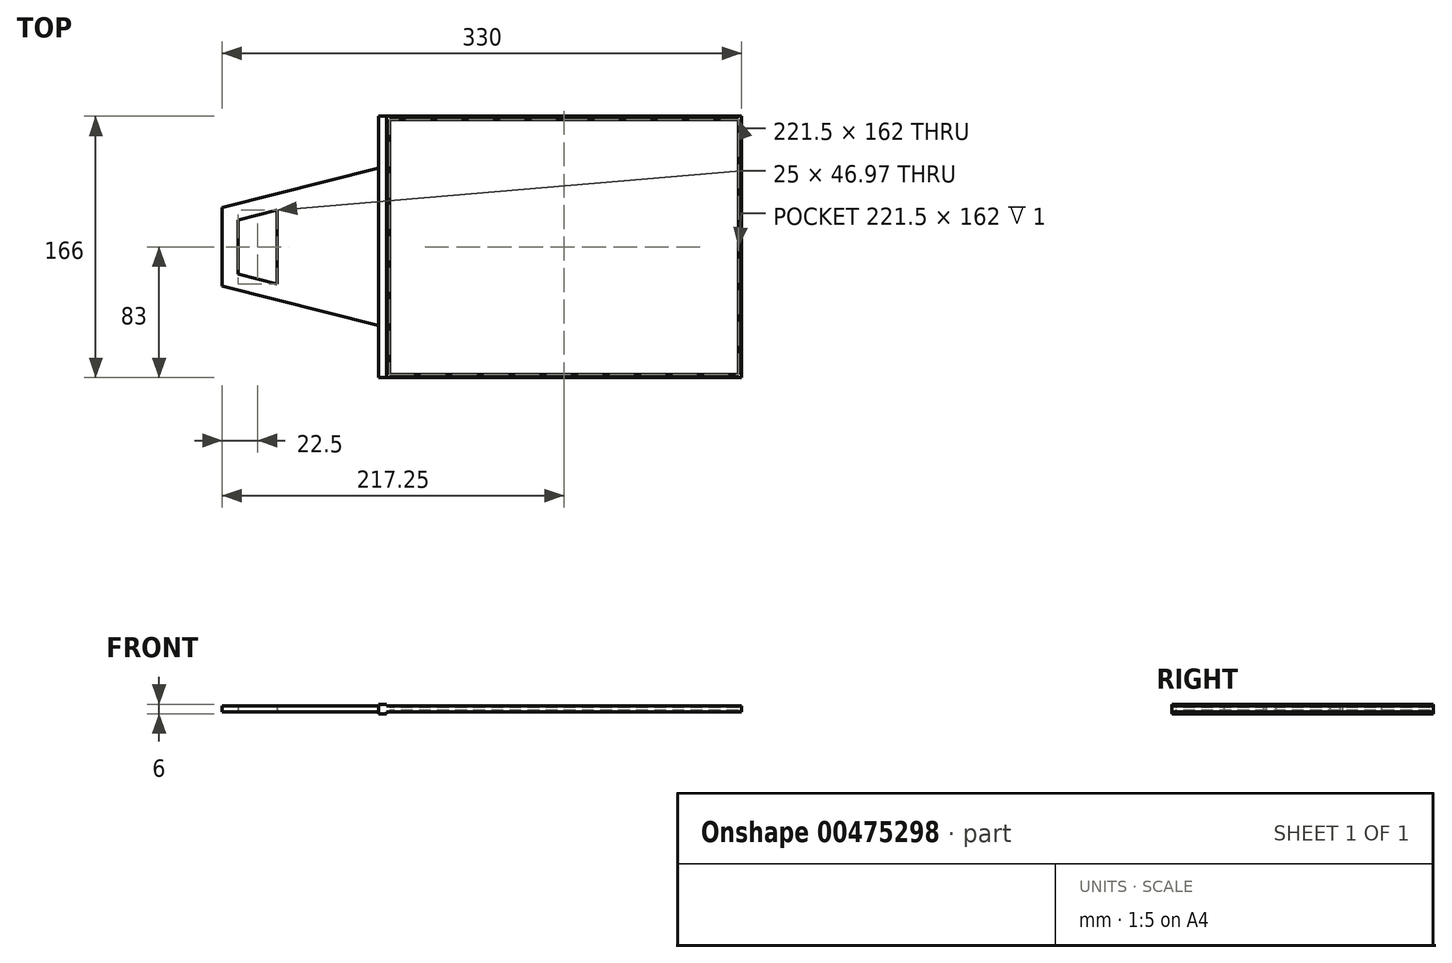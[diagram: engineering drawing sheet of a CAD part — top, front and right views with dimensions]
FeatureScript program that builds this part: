
annotation { "Feature Type Name" : "Feature", "Feature Type Description" : "" }
export const myFeature = defineFeature(function(context is Context, id is Id, definition is map)
    precondition{}
    {
        {
            var Q0;
            Q0=qCreatedBy(makeId("Top.planeOp"),FACE);
            var sketch = newSketch(context, id + "F0", { "sketchPlane" : qUnion([Q0])});
            skLineSegment(sketch, "E0.bottom", {"start": v(112.75, 83) * mm, "end": v(-112.75, 83) * mm});
            skLineSegment(sketch, "E0.top", {"start": v(112.75, -83) * mm, "end": v(-112.75, -83) * mm});
            skLineSegment(sketch, "E0.left", {"start": v(112.75, 83) * mm, "end": v(112.75, -83) * mm});
            skLineSegment(sketch, "E0.right", {"start": v(-112.75, 83) * mm, "end": v(-112.75, -83) * mm});
            skPoint(sketch, "E0.middle", {"position": v(0, 0) * mm});
            skLineSegment(sketch, "E1.bottom", {"start": v(110.75, 81) * mm, "end": v(-110.75, 81) * mm});
            skLineSegment(sketch, "E1.top", {"start": v(110.75, -81) * mm, "end": v(-110.75, -81) * mm});
            skLineSegment(sketch, "E1.left", {"start": v(110.75, 81) * mm, "end": v(110.75, -81) * mm});
            skLineSegment(sketch, "E1.right", {"start": v(-110.75, 81) * mm, "end": v(-110.75, -81) * mm});
            skLineSegment(sketch, "E2", {"start": v(-112.75, 83) * mm, "end": v(-117.75, 83) * mm});
            skLineSegment(sketch, "E3", {"start": v(-117.75, 83) * mm, "end": v(-117.75, -83) * mm});
            skLineSegment(sketch, "E4", {"start": v(-117.75, -83) * mm, "end": v(-112.75, -83) * mm});
            skLineSegment(sketch, "E5", {"start": v(-117.75, 50) * mm, "end": v(-217.25, 25) * mm});
            skLineSegment(sketch, "E6", {"start": v(-217.25, 25) * mm, "end": v(-217.25, -25) * mm});
            skLineSegment(sketch, "E7", {"start": v(-217.25, -25) * mm, "end": v(-117.75, -50) * mm});
            skLineSegment(sketch, "E8.0", {"start": v(-207.25, -17.2) * mm, "end": v(-182.25, -23.48) * mm});
            skLineSegment(sketch, "E8.1", {"start": v(-207.25, 17.2) * mm, "end": v(-207.25, -17.2) * mm});
            skLineSegment(sketch, "E9", {"start": v(-182.25, -23.48) * mm, "end": v(-182.25, 23.48) * mm});
            skLineSegment(sketch, "E10.trimOffspring", {"start": v(-182.25, 23.48) * mm, "end": v(-207.25, 17.2) * mm});
            skSolve(sketch);
        }
        {
            var Q0;
            Q0=makeQuery(id+"F0.imprint","IMPRINT",FACE,{"disambiguationData":[TD([[makeQuery(id+"F0.imprint","IMPRINT",EDGE,{"derivedFrom":sQuery(id+"F0.wireOp",EDGE,"E1.bottom")}),1.0]])]});
            extrude(context, id + "F1", {"entities" : qUnion([Q0]), "endBound" : BoundingType.SYMMETRIC, "depth" : 2 * mm});
        }
        {
            var Q0;
            Q0=makeQuery(id+"F0.imprint","IMPRINT",FACE,{"disambiguationData":[TD([[makeQuery(id+"F0.imprint","IMPRINT",EDGE,{"derivedFrom":sQuery(id+"F0.wireOp",EDGE,"E0.bottom")}),1.0]])]});
            extrude(context, id + "F2", {"entities" : qUnion([Q0]), "operationType" : NewBodyOperationType.ADD, "endBound" : BoundingType.SYMMETRIC, "depth" : 4 * mm});
        }
        {
            var Q0;
            Q0=makeQuery(id+"F0.imprint","IMPRINT",FACE,{"disambiguationData":[TD([[makeQuery(id+"F0.imprint","IMPRINT",EDGE,{"derivedFrom":sQuery(id+"F0.wireOp",EDGE,"E0.right")}),-1.0]])]});
            extrude(context, id + "F3", {"entities" : qUnion([Q0]), "operationType" : NewBodyOperationType.ADD, "endBound" : BoundingType.SYMMETRIC, "depth" : 6 * mm});
        }
        {
            var Q0;
            {var subQ0=sQuery(id+"F0.wireOp",EDGE,"E5");Q0=makeQuery(id+"F0.imprint","IMPRINT",FACE,{"disambiguationData":[TD([[makeQuery(id+"F0.imprint","IMPRINT",EDGE,{"derivedFrom":subQ0}),1.0]])]});}
            extrude(context, id + "F4", {"entities" : qUnion([Q0]), "operationType" : NewBodyOperationType.ADD, "endBound" : BoundingType.SYMMETRIC, "depth" : 4 * mm});
        }
    });
